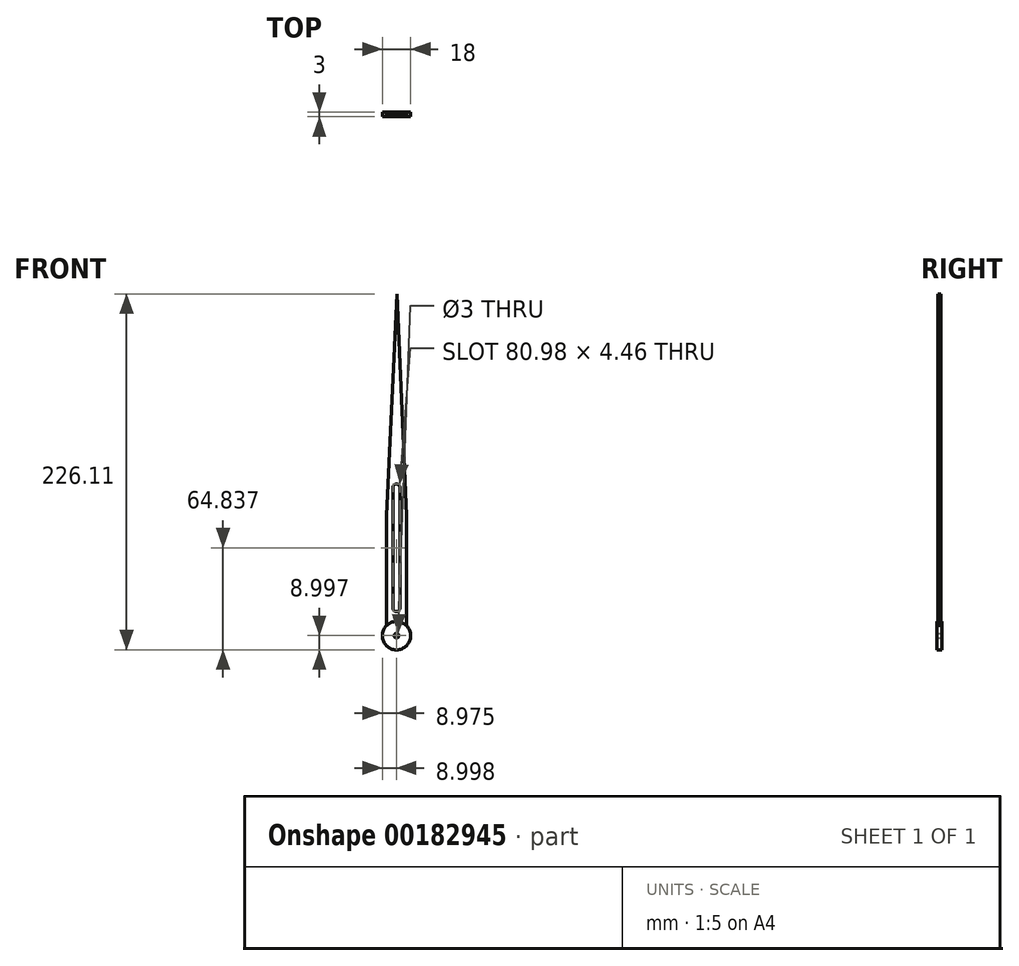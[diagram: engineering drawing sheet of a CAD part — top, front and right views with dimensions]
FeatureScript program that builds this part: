
annotation { "Feature Type Name" : "Feature", "Feature Type Description" : "" }
export const myFeature = defineFeature(function(context is Context, id is Id, definition is map)
    precondition{}
    {
        {
            var Q0;
            Q0=qCreatedBy(makeId("Front.planeOp"),FACE);
            var sketch = newSketch(context, id + "F0", { "sketchPlane" : qUnion([Q0])});
            skCircle(sketch, "E0", {"center": v(-20.04, -44.31) * mm, "radius": 1.5 * mm});
            skCircle(sketch, "E1", {"center": v(-20.04, -44.31) * mm, "radius": 9 * mm});
            skLineSegment(sketch, "E2.left", {"start": v(-26.41, -37.96) * mm, "end": v(-26.41, 32.04) * mm});
            skLineSegment(sketch, "E3.MirrorCS", {"start": v(-13.67, -37.96) * mm, "end": v(-13.67, 32.04) * mm});
            skArc(sketch, "E4", {"start": v(-22.3, -27.34) * mm, "mid": v(-20.02, -28.97) * mm, "end": v(-17.83, -27.21) * mm});
            skArc(sketch, "E5", {"start": v(-17.83, 49.79) * mm, "mid": v(-20.13, 52.02) * mm, "end": v(-22.3, 49.66) * mm});
            skLineSegment(sketch, "E6.MirrorCS", {"start": v(-22.3, 49.66) * mm, "end": v(-22.3, -27.34) * mm});
            skLineSegment(sketch, "E7", {"start": v(-17.83, 49.79) * mm, "end": v(-17.83, -27.21) * mm});
            skLineSegment(sketch, "E8", {"start": v(-19.75, 172.8) * mm, "end": v(-26.41, 32.04) * mm});
            skLineSegment(sketch, "E9.MirrorCS", {"start": v(-19.75, 172.8) * mm, "end": v(-13.67, 32.04) * mm});
            skSolve(sketch);
        }
        {
            var Q0;
            Q0=makeQuery(id+"F0.imprint","IMPRINT",FACE,{"disambiguationData":[TD([[makeQuery(id+"F0.imprint","IMPRINT",EDGE,{"derivedFrom":sQuery(id+"F0.wireOp",EDGE,"E0")}),-1.0]])]});
            var Q1;
            Q1=sQuery(id+"F0.wireOp",EDGE,"p5VHldXC-XaDy-Jo6Q-gzRM-BKwmdG1nrnMR");
            var Q2;
            Q2=sQuery(id+"F0.wireOp",EDGE,"WyDkhZpA-9s04-8oUv-ohR5-d8g4u36zodpv");
            var Q3;
            Q3=sQuery(id+"F0.wireOp",EDGE,"zPygVgP6-IXea-uzZJ-7nVa-Sz4MqIU0xlYZ");
            extrude(context, id + "F1", {"entities" : qUnion([Q0]), "surfaceEntities" : qUnion([Q1, Q2, Q3]), "endBound" : BoundingType.SYMMETRIC, "depth" : 3 * mm});
        }
        {
            var Q0;
            Q0=makeQuery(id+"F0.imprint","IMPRINT",FACE,{"disambiguationData":[TD([[makeQuery(id+"F0.imprint","IMPRINT",EDGE,{"derivedFrom":sQuery(id+"F0.wireOp",EDGE,"64VVkBTR-3lK9-xNKO-ebiv-tDq6J559YHrB.left")}),-1.0]])]});
            var Q1;
            {var subQ4=sQuery(id+"F0.wireOp",EDGE,"E2.left");Q1=makeQuery(id+"F0.imprint","IMPRINT",FACE,{"disambiguationData":[TD([[makeQuery(id+"F0.imprint","IMPRINT",EDGE,{"derivedFrom":subQ4}),-1.0]])]});}
            extrude(context, id + "F2", {"entities" : qUnion([Q0, Q1]), "operationType" : NewBodyOperationType.ADD, "endBound" : BoundingType.SYMMETRIC, "depth" : 2 * mm});
        }
    });
